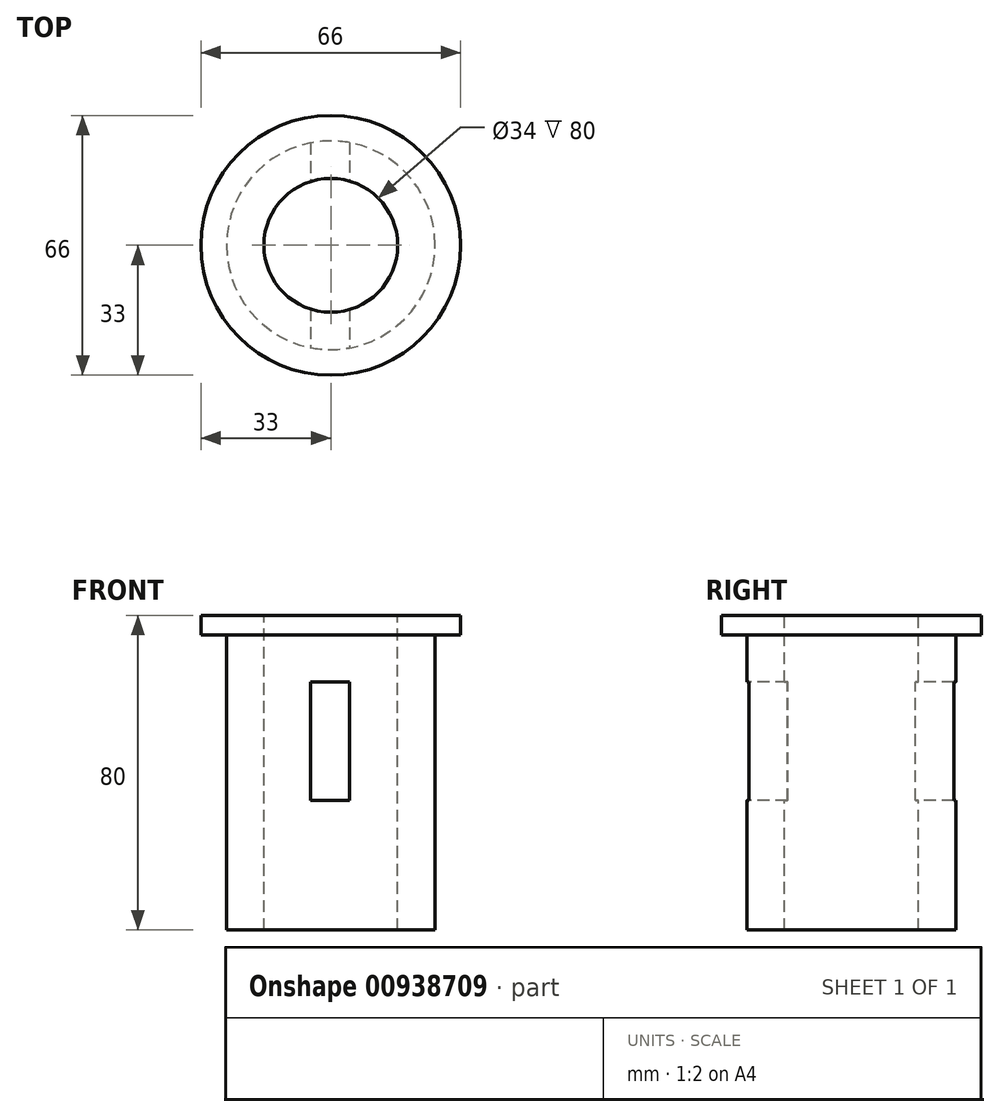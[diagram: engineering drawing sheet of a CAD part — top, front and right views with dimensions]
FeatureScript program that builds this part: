
annotation { "Feature Type Name" : "Feature", "Feature Type Description" : "" }
export const myFeature = defineFeature(function(context is Context, id is Id, definition is map)
    precondition{}
    {
        {
            var Q0;
            Q0=qCreatedBy(makeId("Top.planeOp"),FACE);
            var sketch = newSketch(context, id + "F0", { "sketchPlane" : qUnion([Q0])});
            skCircle(sketch, "E0", {"center": v(0, 0) * mm, "radius": 33 * mm});
            skCircle(sketch, "E1", {"center": v(0, 0) * mm, "radius": 26.5 * mm});
            skCircle(sketch, "E2", {"center": v(0, 0) * mm, "radius": 17 * mm});
            skSolve(sketch);
        }
        {
            var Q0;
            Q0=makeQuery(id+"F0.imprint","IMPRINT",FACE,{"disambiguationData":[TD([[makeQuery(id+"F0.imprint","IMPRINT",EDGE,{"derivedFrom":sQuery(id+"F0.wireOp",EDGE,"E0")}),1.0]])]});
            extrude(context, id + "F1", {"entities" : qUnion([Q0]), "oppositeDirection" : true, "depth" : 5 * mm, "offsetDistance" : 25 * mm});
        }
        {
            var Q0;
            Q0=makeQuery(id+"F0.imprint","IMPRINT",FACE,{"disambiguationData":[TD([[makeQuery(id+"F0.imprint","IMPRINT",EDGE,{"derivedFrom":sQuery(id+"F0.wireOp",EDGE,"E1")}),1.0]])]});
            extrude(context, id + "F2", {"entities" : qUnion([Q0]), "operationType" : NewBodyOperationType.ADD, "oppositeDirection" : true, "depth" : 80 * mm, "offsetDistance" : 25 * mm});
        }
        {
            var Q0;
            Q0=qCreatedBy(makeId("Front.planeOp"),FACE);
            var sketch = newSketch(context, id + "F3", { "sketchPlane" : qUnion([Q0])});
            skLineSegment(sketch, "E3.bottom", {"start": v(4.82, -47) * mm, "end": v(-5.18, -47) * mm});
            skLineSegment(sketch, "E3.top", {"start": v(4.82, -17) * mm, "end": v(-5.18, -17) * mm});
            skLineSegment(sketch, "E3.left", {"start": v(4.82, -47) * mm, "end": v(4.82, -17) * mm});
            skLineSegment(sketch, "E3.right", {"start": v(-5.18, -47) * mm, "end": v(-5.18, -17) * mm});
            skLineSegment(sketch, "E4", {"start": v(0, 0) * mm, "end": v(0, -47) * mm});
            skSolve(sketch);
        }
        {
            var Q0;
            Q0 = qSketchRegion(id + "F3", true);
            extrude(context, id + "F4", {"entities" : qUnion([Q0]), "operationType" : NewBodyOperationType.REMOVE, "endBound" : BoundingType.SYMMETRIC, "oppositeDirection" : true, "depth" : 100 * mm, "offsetDistance" : 25 * mm});
        }
    });
